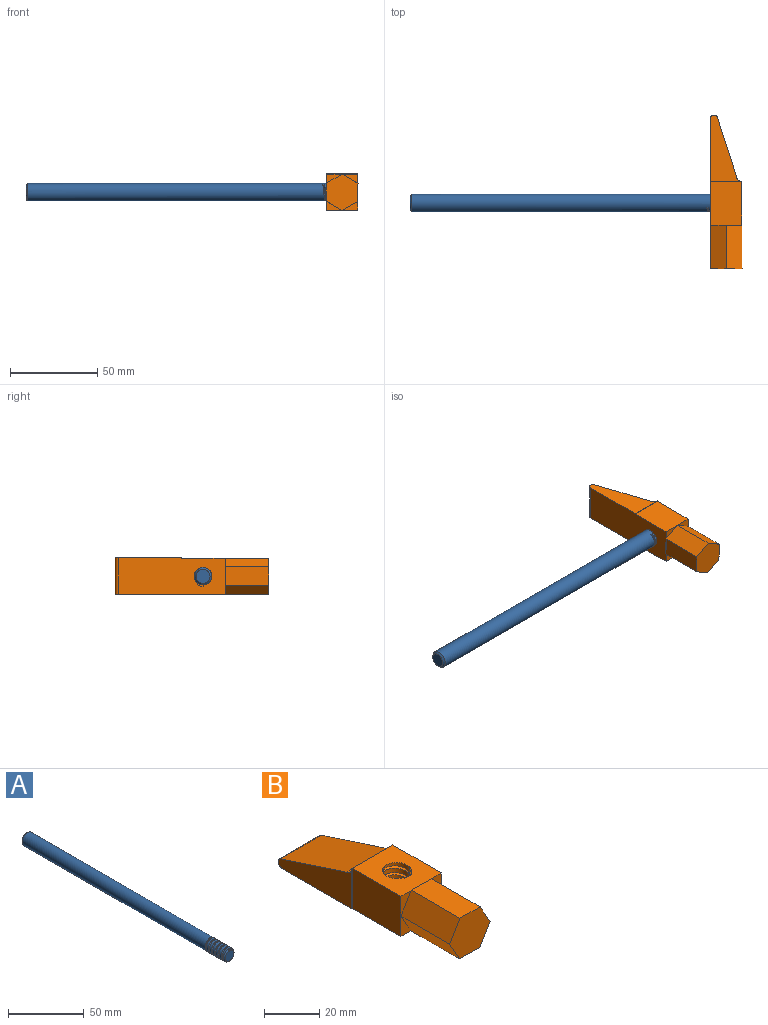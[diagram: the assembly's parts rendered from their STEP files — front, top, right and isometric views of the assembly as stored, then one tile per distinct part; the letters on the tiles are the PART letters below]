
ASSEMBLY  parts=2 mates=1
PART A: 15 faces, bbox 10x190.5x11.5 mm
  f0: cylinder r=5mm len=173mm, axis (0,1,0), area 5377.4mm2, adj f1,f11,f12,f13,f14
  f1: cylinder r=5mm len=10mm, axis (0,1,0), area 62.8mm2, adj f0,f2,f13,f14
  f2: cylinder r=5mm len=10mm, axis (0,1,0), area 62.8mm2, adj f1,f3,f13,f14
  f3: cylinder r=5mm len=10mm, axis (0,1,0), area 62.9mm2, adj f2,f4,f13,f14
  f4: cylinder r=5mm len=10mm, axis (0,1,0), area 62.8mm2, adj f3,f5,f13,f14
  f5: cylinder r=5mm len=10mm, axis (0,1,0), area 62.8mm2, adj f4,f6,f13,f14
  f6: cylinder r=5mm len=10mm, axis (0,1,0), area 21mm2, adj f5,f9,f10,f14
  f7: plane 8x8mm, normal (0,-1,0), area 50.3mm2, adj f10
  f8: plane 8x8mm, normal (0,1,0), area 50.3mm2, adj f11
  f9: cone r=4mm half-angle=45deg, axis (0,1,0), area 2.2mm2, adj f6,f10,f13
  f10: cone r=4mm half-angle=45deg, axis (0,1,0), area 31.8mm2, adj f6,f7,f9,f14
  f11: cone r=5mm half-angle=45deg, axis (0,-1,0), area 40mm2, adj f0,f8
  f12: plane 1x0.75mm, normal (0.87,0,0.5), area 0.4mm2, adj f0,f13,f14
  f13: bspline ~20.5x11.55mm, area 184.1mm2, adj f0,f1,f2,f3,f4,f5,f9,f12
  f14: bspline ~20.5x11.55mm, area 179.9mm2, adj f0,f1,f2,f3,f4,f5,f6,f10
PART B: 26 faces, bbox 21.3x88.3x18.9 mm
  f0: plane 10.46x0.11mm, normal (0,1,0), area 0.6mm2, adj f1,f2,f14
  f1: plane 25x10.39mm, normal (-0.01,0,-1), area 259.8mm2, adj f0,f2,f6,f7
  f2: plane 25x8.94mm, normal (0.86,0,-0.51), area 259.8mm2, adj f0,f1,f3,f7,f16
  f3: plane 25x9.06mm, normal (0.87,0,0.49), area 259.8mm2, adj f2,f4,f7,f11
  f4: plane 25x10.39mm, normal (0.01,0,1), area 259.8mm2, adj f3,f5,f7,f8
  f5: plane 25x8.94mm, normal (-0.86,0,0.51), area 259.8mm2, adj f4,f6,f7,f8,f10
  f6: plane 25x9.06mm, normal (-0.87,0,-0.49), area 259.8mm2, adj f1,f5,f7,f9
  f7: plane 20.78x18.11mm, normal (0,-1,0), area 280.6mm2, adj f1,f2,f3,f4,f5,f6
  f8: plane 10.46x0.11mm, normal (0,1,0), area 0.6mm2, adj f4,f5,f12
  f9: plane 9.06x5.1mm, normal (0,-1,0), area 23.1mm2, adj f6,f14,f15
  f10: plane 8.83x5.23mm, normal (0,-1,0), area 23.1mm2, adj f5,f12,f15
  f11: plane 9.06x5.1mm, normal (0,-1,0), area 23.1mm2, adj f3,f12,f13
  f12: plane 25.32x21.1mm, normal (0,0,1), area 436.2mm2, adj f8,f10,f11,f13,f15,f20,f22,f24
  f13: plane 63x17.88mm, normal (1,0,0), area 811.8mm2, adj f11,f12,f14,f16,f18,f19,f20
  f14: plane 61x21mm, normal (0,0,-1), area 1197mm2, adj f0,f9,f13,f15,f16,f17,f18,f21
  f15: plane 25x17.88mm, normal (-1,0,0), area 447.1mm2, adj f9,f10,f12,f14,f17
  f16: plane 8.83x5.23mm, normal (0,-1,0), area 23.1mm2, adj f2,f13,f14
  f17: plane 17.88x0.22mm, normal (0,-1,0), area 3.9mm2, adj f14,f15,f20,f21
  f18: cylinder r=2mm len=21mm, axis (1,0,0), area 118.8mm2, adj f13,f14,f19,f21
  f19: plane 33.95x21mm, normal (0,0.31,0.95), area 749.5mm2, adj f13,f18,f20,f21
  f20: cylinder r=3mm len=21mm, axis (1,0,0), area 91.8mm2, adj f12,f13,f17,f19,f21
  f21: plane 38x17.88mm, normal (-1,0,0), area 364.7mm2, adj f14,f17,f18,f19,f20
  f22: cylinder r=5mm len=17.88mm, axis (0,0,1), area 376.2mm2, adj f12,f14,f23,f24,f25
  f23: plane 0.96x0.87mm, normal (0,1,0), area 0.4mm2, adj f14,f22,f24,f25
  f24: bspline ~18.5x13.55mm, area 201.5mm2, adj f12,f14,f22,f23,f25
  f25: bspline ~18x13.55mm, area 196mm2, adj f12,f22,f23,f24
PLACE A rot(axis=(0.71,-0.71,0),180deg) t=(-152.42,1.92,54.98)mm
PLACE B rot(axis=(0,1,0),90deg) t=(28.64,-10.77,54.98)mm
MATE slider A.f0 <-> B.f22  axis (1,0,0) through (37.58,1.92,54.98)mm
